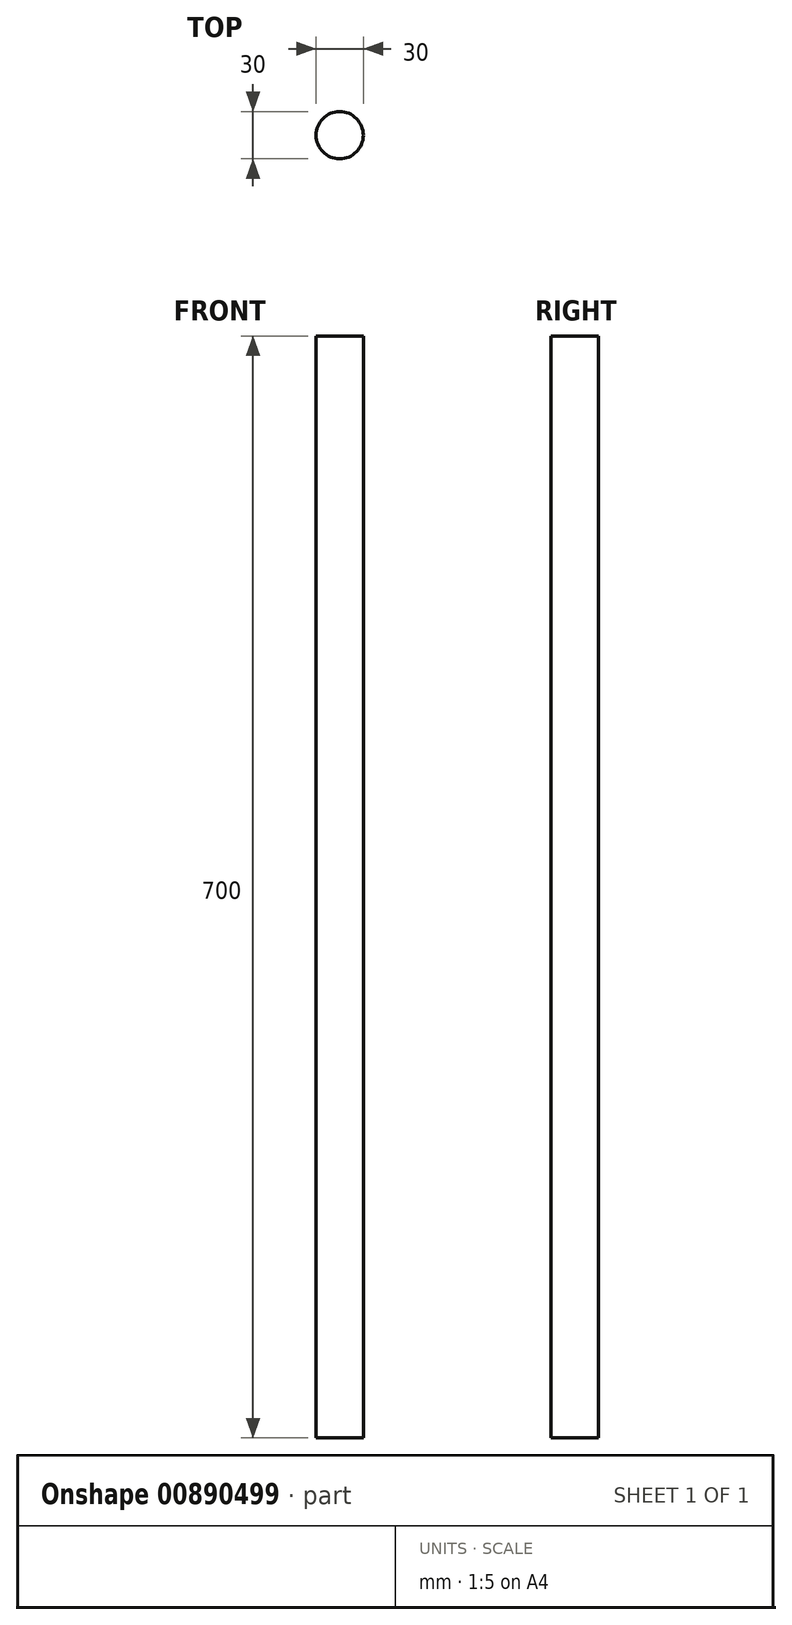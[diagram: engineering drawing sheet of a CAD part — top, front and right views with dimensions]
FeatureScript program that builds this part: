
annotation { "Feature Type Name" : "Feature", "Feature Type Description" : "" }
export const myFeature = defineFeature(function(context is Context, id is Id, definition is map)
    precondition{}
    {
        {
            var Q0;
            Q0=qCreatedBy(makeId("Top.planeOp"),FACE);
            var sketch = newSketch(context, id + "F0", { "sketchPlane" : qUnion([Q0])});
            skCircle(sketch, "E0", {"center": v(0, 0) * mm, "radius": 15 * mm});
            skSolve(sketch);
        }
        {
            var Q0;
            Q0 = qSketchRegion(id + "F0", true);
            extrude(context, id + "F1", {"entities" : qUnion([Q0]), "depth" : 700 * mm, "offsetDistance" : 25 * mm});
        }
    });
